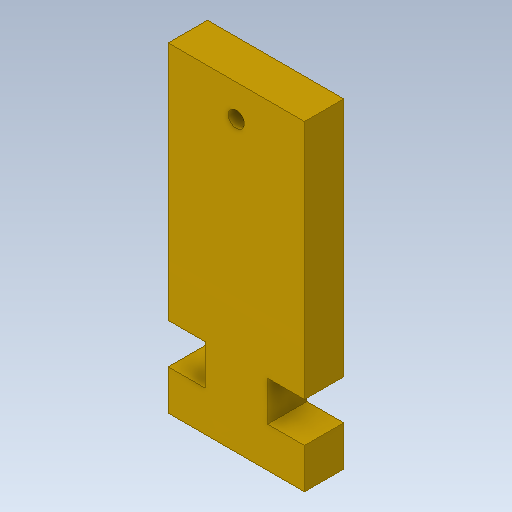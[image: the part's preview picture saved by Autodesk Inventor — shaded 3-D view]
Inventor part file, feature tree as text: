
AUTODESK INVENTOR PART (.ipt)
format: ipt  version: 2020 (Build 240168000, 168)  size: 95,744 bytes
history: native  units: mm
features: other x1, extrude x1, sketch x1
ambient origin geometry x8: Origin, YZ Plane, XZ Plane, XY Plane, X Axis, Y Axis, Z Axis, Center Point
bodies: Body1 (feature_tree)
feature tree (3):
  other  "Твердое тело1"
  extrude  "Выдавливание1"  Depth=4.9mm TaperAngle=0.0deg
  sketch  "Эскиз1"
